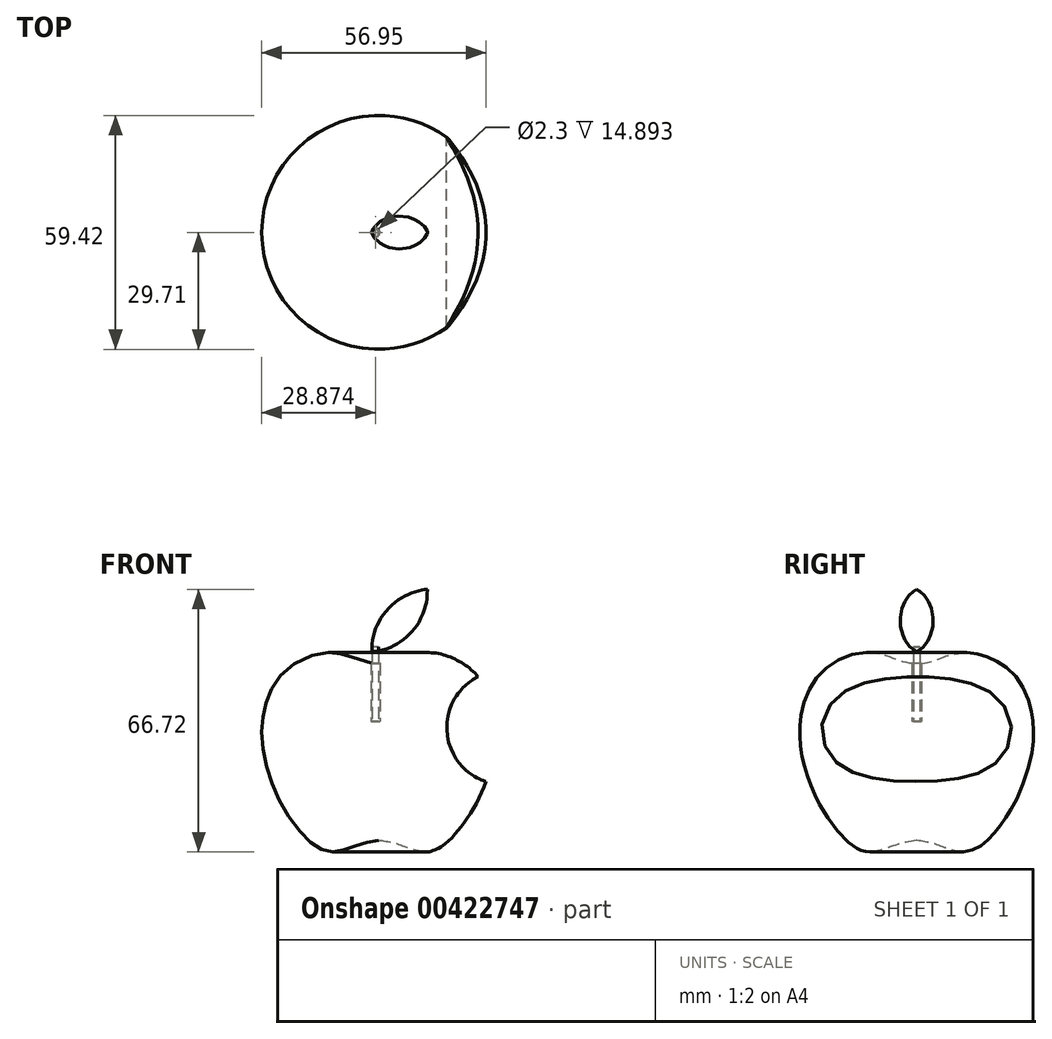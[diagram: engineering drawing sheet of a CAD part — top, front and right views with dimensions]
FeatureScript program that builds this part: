
annotation { "Feature Type Name" : "Feature", "Feature Type Description" : "" }
export const myFeature = defineFeature(function(context is Context, id is Id, definition is map)
    precondition{}
    {
        {
            var Q0;
            Q0=qCreatedBy(makeId("Front.planeOp"),FACE);
            var sketch = newSketch(context, id + "F0", { "sketchPlane" : qUnion([Q0])});
            skLineSegment(sketch, "E0.bottom", {"start": v(-36.6, 35.25) * mm, "end": v(33.4, 35.25) * mm});
            skLineSegment(sketch, "E0.top", {"start": v(-36.6, -34.75) * mm, "end": v(33.4, -34.75) * mm});
            skLineSegment(sketch, "E0.left", {"start": v(-36.6, 35.25) * mm, "end": v(-36.6, -34.75) * mm});
            skLineSegment(sketch, "E0.right", {"start": v(33.4, 35.25) * mm, "end": v(33.4, -34.75) * mm});
            skSolve(sketch);
        }
        {
            var Q0;
            Q0=qCreatedBy(makeId("Front.planeOp"),FACE);
            var sketch = newSketch(context, id + "F1", { "sketchPlane" : qUnion([Q0])});
            skFitSpline(sketch, "E1", {"points": [v(0, 14.81) * mm, v(-7.24, 16.58) * mm, v(-10.26, 17.34) * mm, v(-15.24, 17.3) * mm, v(-22.97, 13.65) * mm, v(-27.07, 8.6) * mm, v(-28.92, 3.7) * mm, v(-29.66, -1.02) * mm, v(-29.31, -7.62) * mm, v(-27.32, -15) * mm, v(-24.16, -21.98) * mm, v(-19.39, -28.63) * mm, v(-15.95, -31.73) * mm, v(-12.68, -33.07) * mm, v(-10.1, -32.9) * mm, v(-6.36, -31.73) * mm, v(-3.48, -30.8) * mm, v(0, -30.2) * mm, v(0, -30.31) * mm], "startDerivative": vector(-103.56, -11.65) * mm, "endDerivative": vector(0, -38.55) * mm});
            skLineSegment(sketch, "E2", {"start": v(0, 14.81) * mm, "end": v(0, -30.2) * mm});
            skPoint(sketch, "E3", {"position": v(-4.69, 15.62) * mm});
            skSolve(sketch);
        }
        {
            var Q0;
            Q0 = qSketchRegion(id + "F1", true);
            var Q1;
            Q1=sQuery(id+"F1.wireOp",EDGE,"E2");
            revolve(context, id + "F2", {"entities" : qUnion([Q0]), "axis" : qUnion([Q1]), "revolveType" : RevolveType.FULL});
        }
        {
            var Q0;
            Q0=qCreatedBy(makeId("Front.planeOp"),FACE);
            var sketch = newSketch(context, id + "F3", { "sketchPlane" : qUnion([Q0])});
            skArc(sketch, "E4", {"start": v(25.33, 11.44) * mm, "mid": v(17.33, -2.62) * mm, "end": v(27.41, -15.27) * mm});
            skArc(sketch, "E5", {"start": v(27.41, -15.27) * mm, "mid": v(38.74, -0.95) * mm, "end": v(25.33, 11.44) * mm});
            skSolve(sketch);
        }
        {
            var Q0;
            Q0 = qSketchRegion(id + "F3", true);
            extrude(context, id + "F4", {"entities" : qUnion([Q0]), "endBound" : BoundingType.SYMMETRIC, "depth" : 70 * mm});
        }
        {
            var Q0;
            Q0=makeQuery(id+"F4.opExtrude","SWEPT_BODY",BODY,{"disambiguationData":[OSD([sQuery(id+"F3.wireOp",EDGE,"E4"),sQuery(id+"F3.wireOp",EDGE,"E5")])]});
            var Q1;
            Q1=makeQuery(id+"F2.opRevolve","SWEPT_BODY",BODY,{"disambiguationData":[OSD([sQuery(id+"F1.wireOp",EDGE,"E1"),sQuery(id+"F1.wireOp",EDGE,"E2")])]});
            booleanBodies(context, id + "F5", {"operationType" : BooleanOperationType.SUBTRACTION, "tools" : qUnion([Q0]), "targets" : qUnion([Q1])});
        }
        {
            var Q0;
            Q0=makeQuery(id+"F0.imprint","IMPRINT",FACE,{"disambiguationData":[TD([[makeQuery(id+"F0.imprint","IMPRINT",EDGE,{"derivedFrom":sQuery(id+"F0.wireOp",EDGE,"E0.bottom")}),-1.0]])]});
            var sketch = newSketch(context, id + "F6", { "sketchPlane" : qUnion([Q0])});
            skFitSpline(sketch, "E6", {"points": [v(-1.59, 17.88) * mm, v(-1.68, 19.06) * mm, v(-1.47, 21.11) * mm, v(-1, 23.04) * mm, v(-0.34, 24.55) * mm, v(0.58, 26.3) * mm, v(2.12, 28.35) * mm, v(3.72, 30.01) * mm, v(5.33, 31.11) * mm, v(7.08, 32.13) * mm, v(8.59, 32.8) * mm, v(10.15, 33.24) * mm, v(11.48, 33.5) * mm, v(12.34, 33.6) * mm], "startDerivative": vector(-2.15, 17.36) * mm, "endDerivative": vector(15.13, 1.45) * mm});
            skLineSegment(sketch, "E7", {"start": v(-1.59, 17.88) * mm, "end": v(12.34, 33.6) * mm});
            skSolve(sketch);
        }
        {
            var Q0;
            Q0 = qSketchRegion(id + "F6", true);
            var Q1;
            Q1=sQuery(id+"F6.wireOp",EDGE,"E7");
            revolve(context, id + "F7", {"entities" : qUnion([Q0]), "axis" : qUnion([Q1]), "revolveType" : RevolveType.FULL});
        }
        {
            var Q0;
            Q0=qCreatedBy(makeId("Top.planeOp"),FACE);
            var sketch = newSketch(context, id + "F8", { "sketchPlane" : qUnion([Q0])});
            skCircle(sketch, "E8", {"center": v(-0.84, 0) * mm, "radius": 0.84 * mm});
            skSolve(sketch);
        }
        {
            var Q0;
            Q0 = qSketchRegion(id + "F8", true);
            extrude(context, id + "F9", {"entities" : qUnion([Q0]), "depth" : 19 * mm});
        }
        {
            var Q0;
            Q0=qCreatedBy(makeId("Top.planeOp"),FACE);
            var sketch = newSketch(context, id + "F10", { "sketchPlane" : qUnion([Q0])});
            skCircle(sketch, "E9", {"center": v(-0.84, 0) * mm, "radius": 1.15 * mm});
            skSolve(sketch);
        }
        {
            var Q0;
            Q0 = qSketchRegion(id + "F10", true);
            extrude(context, id + "F11", {"entities" : qUnion([Q0]), "depth" : 25 * mm});
        }
        {
            var Q0;
            Q0=makeQuery(id+"F11.opExtrude","SWEPT_BODY",BODY,{"disambiguationData":[OSD([sQuery(id+"F10.wireOp",EDGE,"E9")])]});
            var Q1;
            Q1=makeQuery(id+"F2.opRevolve","SWEPT_BODY",BODY,{"disambiguationData":[OSD([sQuery(id+"F1.wireOp",EDGE,"E1"),sQuery(id+"F1.wireOp",EDGE,"E2")])]});
            booleanBodies(context, id + "F12", {"operationType" : BooleanOperationType.SUBTRACTION, "tools" : qUnion([Q0]), "targets" : qUnion([Q1])});
        }
    });
